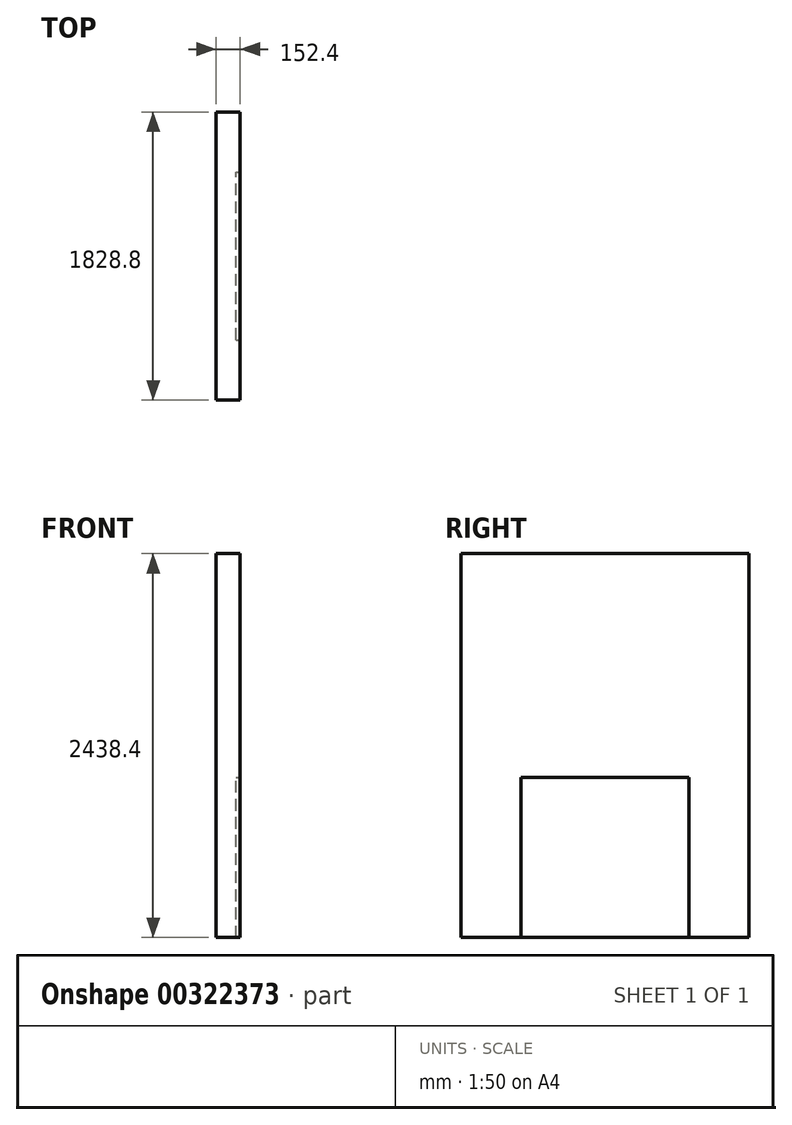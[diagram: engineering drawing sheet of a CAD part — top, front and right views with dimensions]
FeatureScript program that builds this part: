
annotation { "Feature Type Name" : "Feature", "Feature Type Description" : "" }
export const myFeature = defineFeature(function(context is Context, id is Id, definition is map)
    precondition{}
    {
        {
            var Q0;
            Q0=qCreatedBy(makeId("Right.planeOp"),FACE);
            var sketch = newSketch(context, id + "F0", { "sketchPlane" : qUnion([Q0])});
            skLineSegment(sketch, "E0.bottom", {"start": v(-914.4, 1219.2) * mm, "end": v(914.4, 1219.2) * mm});
            skLineSegment(sketch, "E0.top", {"start": v(-914.4, -1219.2) * mm, "end": v(914.4, -1219.2) * mm});
            skLineSegment(sketch, "E0.left", {"start": v(-914.4, 1219.2) * mm, "end": v(-914.4, -1219.2) * mm});
            skLineSegment(sketch, "E0.right", {"start": v(914.4, 1219.2) * mm, "end": v(914.4, -1219.2) * mm});
            skSolve(sketch);
        }
        {
            var Q0;
            Q0=makeQuery(id+"F0.imprint","IMPRINT",FACE,{"disambiguationData":[TD([[makeQuery(id+"F0.imprint","IMPRINT",EDGE,{"derivedFrom":sQuery(id+"F0.wireOp",EDGE,"E0.bottom")}),-1.0]])]});
            extrude(context, id + "F1", {"entities" : qUnion([Q0]), "depth" : 152.4 * mm});
        }
        {
            var Q0;
            Q0=makeQuery(id+"F1.opExtrude","CAP_FACE",FACE,{"disambiguationData":[OSD([sQuery(id+"F0.wireOp",EDGE,"E0.bottom"),sQuery(id+"F0.wireOp",EDGE,"E0.top"),sQuery(id+"F0.wireOp",EDGE,"E0.left"),sQuery(id+"F0.wireOp",EDGE,"E0.right")])],"isStart":false});
            var sketch = newSketch(context, id + "F2", { "sketchPlane" : qUnion([Q0])});
            skLineSegment(sketch, "E1.bottom", {"start": v(-533.4, -1219.2) * mm, "end": v(533.4, -1219.2) * mm});
            skLineSegment(sketch, "E1.top", {"start": v(-533.4, -203.2) * mm, "end": v(533.4, -203.2) * mm});
            skLineSegment(sketch, "E1.left", {"start": v(-533.4, -1219.2) * mm, "end": v(-533.4, -203.2) * mm});
            skLineSegment(sketch, "E1.right", {"start": v(533.4, -1219.2) * mm, "end": v(533.4, -203.2) * mm});
            skSolve(sketch);
        }
        {
            var Q0;
            Q0=makeQuery(id+"F2.imprint","IMPRINT",FACE,{"disambiguationData":[TD([[makeQuery(id+"F2.imprint","IMPRINT",EDGE,{"derivedFrom":sQuery(id+"F2.wireOp",EDGE,"E1.bottom")}),1.0]])]});
            extrude(context, id + "F3", {"entities" : qUnion([Q0]), "operationType" : NewBodyOperationType.REMOVE, "oppositeDirection" : true, "depth" : 25.4 * mm});
        }
    });
